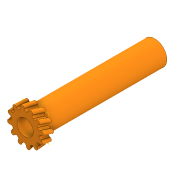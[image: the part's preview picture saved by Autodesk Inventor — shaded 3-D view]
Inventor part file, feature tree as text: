
AUTODESK INVENTOR PART (.ipt)
format: ipt  version: 2020 (Build 240168000, 168)  size: 334,848 bytes
history: native  units: in
note: dims shown in document units (in); Inventor stores cm internally (conversion verified against a paired STEP export)
features: sketch x3, extrude x1, plane x1, sweep x1, other x1
ambient origin geometry x8: Origin, YZ Plane, XZ Plane, XY Plane, X Axis, Y Axis, Z Axis, Center Point
bodies: Solid1 (feature_tree)
feature tree (7):
  extrude  "Extrusion1"  Depth=0.315in
  plane  "Work Plane1"
  sweep  "Sweep1"
  sketch  "Sketch1"  dims[d0=0.4724in d1=0.315in]
  sketch  "Sketch3"  dims[d2=2.5197in d3=0.0in d7=-0.1969in d8=0.7087in d9=0.0866in d10=0.0787in d11=0.0787in d12=0.0787in d13=4.7244in d15=360.0deg d17=0.1969in d18=0.0118in d19=0.535in d20=0.0in d21=0.0in d22=0.0in]
  sketch  "3D Sketch1"
  other  "Helical Curve1"
